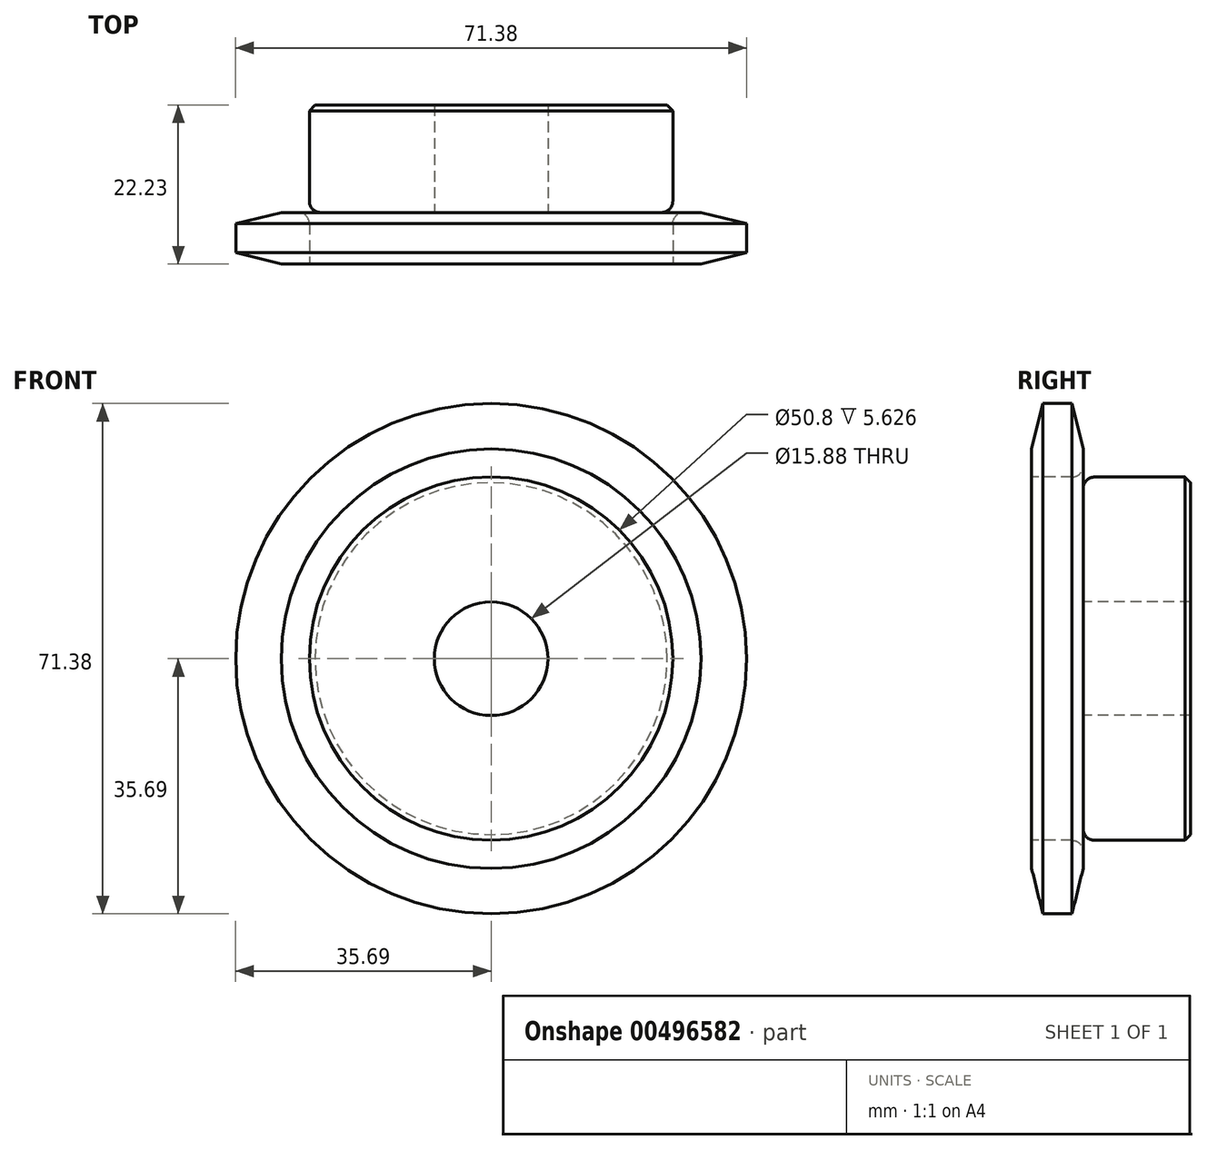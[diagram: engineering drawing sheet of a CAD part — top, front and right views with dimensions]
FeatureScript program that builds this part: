
annotation { "Feature Type Name" : "Feature", "Feature Type Description" : "" }
export const myFeature = defineFeature(function(context is Context, id is Id, definition is map)
    precondition{}
    {
        {
            var Q0;
            Q0=qCreatedBy(makeId("Right.planeOp"),FACE);
            var sketch = newSketch(context, id + "F0", { "sketchPlane" : qUnion([Q0])});
            skLineSegment(sketch, "E0", {"start": v(0, 0) * mm, "end": v(22.23, 0) * mm, "construction": true});
            skLineSegment(sketch, "E1.bottom", {"start": v(0, 7.94) * mm, "end": v(7.21, 7.94) * mm});
            skLineSegment(sketch, "E1.top", {"start": v(0, 35.69) * mm, "end": v(7.21, 35.69) * mm});
            skLineSegment(sketch, "E1.left", {"start": v(0, 7.94) * mm, "end": v(0, 35.69) * mm});
            skLineSegment(sketch, "E1.right", {"start": v(7.21, 7.94) * mm, "end": v(7.21, 35.69) * mm});
            skPoint(sketch, "E2.oppositeSnap0", {"position": v(3.6, 7.94) * mm});
            skLineSegment(sketch, "E2.bottom", {"start": v(0, 25.4) * mm, "end": v(22.23, 25.4) * mm});
            skLineSegment(sketch, "E2.top", {"start": v(0, 7.94) * mm, "end": v(22.23, 7.94) * mm});
            skLineSegment(sketch, "E2.left", {"start": v(0, 25.4) * mm, "end": v(0, 7.94) * mm});
            skLineSegment(sketch, "E2.right", {"start": v(22.23, 25.4) * mm, "end": v(22.23, 7.94) * mm});
            skLineSegment(sketch, "E3.MirrorCS", {"start": v(0, -35.69) * mm, "end": v(7.21, -35.69) * mm});
            skLineSegment(sketch, "E4.MirrorCS", {"start": v(0, -7.94) * mm, "end": v(7.21, -7.94) * mm});
            skPoint(sketch, "E5.MirrorP", {"position": v(3.6, -7.94) * mm});
            skLineSegment(sketch, "E6.MirrorCS", {"start": v(0, -7.94) * mm, "end": v(0, -35.69) * mm});
            skLineSegment(sketch, "E7.MirrorCS", {"start": v(7.21, -7.94) * mm, "end": v(7.21, -35.69) * mm});
            skLineSegment(sketch, "E8.MirrorCS", {"start": v(0, -25.4) * mm, "end": v(22.23, -25.4) * mm});
            skLineSegment(sketch, "E9.MirrorCS", {"start": v(22.23, -25.4) * mm, "end": v(22.23, -7.94) * mm});
            skLineSegment(sketch, "E10.MirrorCS", {"start": v(0, -25.4) * mm, "end": v(0, -7.94) * mm});
            skLineSegment(sketch, "E11.MirrorCS", {"start": v(0, -7.94) * mm, "end": v(22.23, -7.94) * mm});
            skSolve(sketch);
        }
        {
            var Q0;
            {var subQ5=sQuery(id+"F0.wireOp",EDGE,"E2.right");Q0=makeQuery(id+"F0.imprint","IMPRINT",FACE,{"disambiguationData":[TD([[makeQuery(id+"F0.imprint","IMPRINT",EDGE,{"derivedFrom":subQ5}),-1.0]])]});}
            var Q1;
            {var subQ5=sQuery(id+"F0.wireOp",EDGE,"E2.left");Q1=makeQuery(id+"F0.imprint","IMPRINT",FACE,{"disambiguationData":[TD([[makeQuery(id+"F0.imprint","IMPRINT",EDGE,{"derivedFrom":subQ5}),1.0]])]});}
            var Q2;
            {var subQ0=sQuery(id+"F0.wireOp",EDGE,"E1.top");Q2=makeQuery(id+"F0.imprint","IMPRINT",FACE,{"disambiguationData":[TD([[makeQuery(id+"F0.imprint","IMPRINT",EDGE,{"derivedFrom":subQ0}),-1.0]])]});}
            var Q3;
            Q3=sQuery(id+"F0.wireOp",EDGE,"E0");
            revolve(context, id + "F1", {"entities" : qUnion([Q0, Q1, Q2]), "axis" : qUnion([Q3]), "revolveType" : RevolveType.FULL});
        }
        {
            var Q0;
            Q0=makeQuery(id+"F1.opRevolve","SWEPT_EDGE",EDGE,{"disambiguationData":[OSD([sQuery(id+"F0.wireOp",EDGE,"E1.right"),sQuery(id+"F0.wireOp",EDGE,"E2.bottom")])]});
            fillet(context, id + "F2", {"entities" : qUnion([Q0]), "radius" : 1.59 * mm, "tangentPropagation" : true, "allowEdgeOverflow" : false});
        }
        {
            var Q0;
            Q0=makeQuery(id+"F1.opRevolve","SWEPT_EDGE",EDGE,{"disambiguationData":[OSD([sQuery(id+"F0.wireOp",EDGE,"E2.bottom"),sQuery(id+"F0.wireOp",EDGE,"E2.right")])]});
            chamfer(context, id + "F3", {"entities" : qUnion([Q0]), "width" : 0.8 * mm, "tangentPropagation" : true});
        }
        {
            var Q0;
            Q0=makeQuery(id+"F1.opRevolve","SWEPT_FACE",FACE,{"disambiguationData":[OSD([sQuery(id+"F0.wireOp",EDGE,"E1.top")])]});
            chamfer(context, id + "F4", {"entities" : qUnion([Q0]), "chamferType" : ChamferType.TWO_OFFSETS, "width1" : 6.35 * mm, "oppositeDirection" : false, "width2" : 1.57 * mm, "tangentPropagation" : true});
        }
    });
